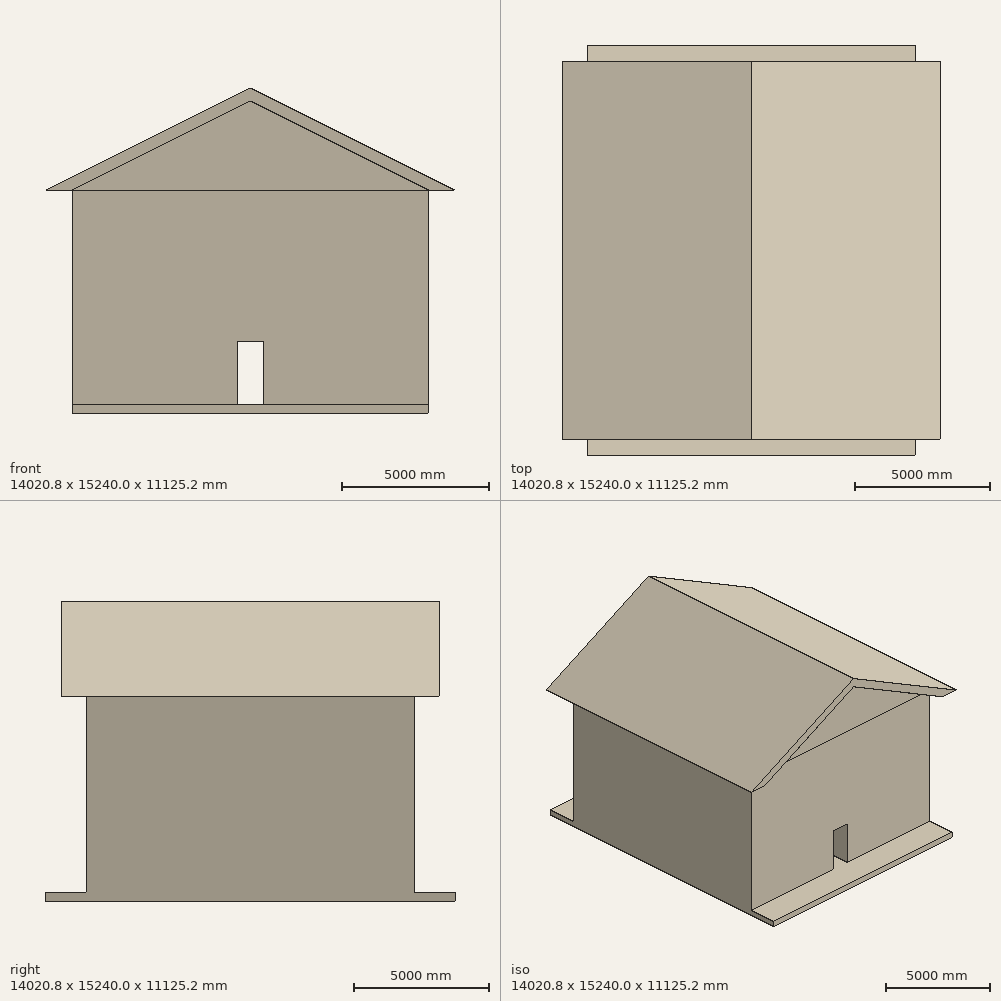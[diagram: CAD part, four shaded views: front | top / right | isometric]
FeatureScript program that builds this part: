
annotation { "Feature Type Name" : "Feature", "Feature Type Description" : "" }
export const myFeature = defineFeature(function(context is Context, id is Id, definition is map)
    precondition{}
    {
        {
            var Q0;
            Q0=qCreatedBy(makeId("Front.planeOp"),FACE);
            var sketch = newSketch(context, id + "F0", { "sketchPlane" : qUnion([Q0])});
            skLineSegment(sketch, "E0", {"start": v(0, 0) * mm, "end": v(-6096, 0) * mm});
            skLineSegment(sketch, "E1", {"start": v(0, 0) * mm, "end": v(6096, 0) * mm});
            skLineSegment(sketch, "E2", {"start": v(0, 0) * mm, "end": v(0, 3048) * mm});
            skLineSegment(sketch, "E3", {"start": v(-6096, 0) * mm, "end": v(0, 3048) * mm});
            skLineSegment(sketch, "E4", {"start": v(6096, 0) * mm, "end": v(0, 3048) * mm});
            skLineSegment(sketch, "E5", {"start": v(-6096, 0) * mm, "end": v(-7010.4, 0) * mm});
            skLineSegment(sketch, "E6", {"start": v(6096, 0) * mm, "end": v(7010.4, 0) * mm});
            skLineSegment(sketch, "E7", {"start": v(0, 3048) * mm, "end": v(0, 3505.2) * mm});
            skLineSegment(sketch, "E8", {"start": v(0, 3505.2) * mm, "end": v(7010.4, 0) * mm});
            skLineSegment(sketch, "E9", {"start": v(0, 3505.2) * mm, "end": v(-7010.4, 0) * mm});
            skLineSegment(sketch, "E10", {"start": v(-6096, 0) * mm, "end": v(-6096, -7315.2) * mm});
            skLineSegment(sketch, "E11", {"start": v(6096, 0) * mm, "end": v(6096, -7315.2) * mm});
            skLineSegment(sketch, "E12", {"start": v(-6096, -7315.2) * mm, "end": v(6096, -7315.2) * mm});
            skLineSegment(sketch, "E13", {"start": v(-6096, -7315.2) * mm, "end": v(-6096, -7620) * mm});
            skLineSegment(sketch, "E14", {"start": v(6096, -7315.2) * mm, "end": v(6096, -7620) * mm});
            skLineSegment(sketch, "E15", {"start": v(6096, -7620) * mm, "end": v(-6096, -7620) * mm});
            skLineSegment(sketch, "E16", {"start": v(0, -7315.2) * mm, "end": v(-457.2, -7315.2) * mm});
            skLineSegment(sketch, "E17", {"start": v(-457.2, -7315.2) * mm, "end": v(0, -7315.2) * mm});
            skLineSegment(sketch, "E18", {"start": v(0, -7315.2) * mm, "end": v(457.2, -7315.2) * mm});
            skLineSegment(sketch, "E19", {"start": v(457.2, -7315.2) * mm, "end": v(457.2, -5181.6) * mm});
            skLineSegment(sketch, "E20", {"start": v(457.2, -5181.6) * mm, "end": v(-457.2, -5181.6) * mm});
            skLineSegment(sketch, "E21", {"start": v(-457.2, -7315.2) * mm, "end": v(-457.2, -5181.6) * mm});
            skSolve(sketch);
        }
        {
            var Q0;
            Q0=makeQuery(id+"F0.imprint","IMPRINT",FACE,{"disambiguationData":[TD([[makeQuery(id+"F0.imprint","IMPRINT",EDGE,{"derivedFrom":sQuery(id+"F0.wireOp",EDGE,"E3")}),1.0]])]});
            var Q1;
            Q1=makeQuery(id+"F0.imprint","IMPRINT",FACE,{"disambiguationData":[TD([[makeQuery(id+"F0.imprint","IMPRINT",EDGE,{"derivedFrom":sQuery(id+"F0.wireOp",EDGE,"E4")}),-1.0]])]});
            extrude(context, id + "F1", {"entities" : qUnion([Q0, Q1]), "endBound" : BoundingType.SYMMETRIC, "depth" : 14020.8 * mm, "offsetDistance" : 30.48 * mm});
        }
        {
            var Q0;
            Q0=makeQuery(id+"F0.imprint","IMPRINT",FACE,{"disambiguationData":[TD([[makeQuery(id+"F0.imprint","IMPRINT",EDGE,{"derivedFrom":sQuery(id+"F0.wireOp",EDGE,"E0")}),1.0]])]});
            extrude(context, id + "F2", {"entities" : qUnion([Q0]), "endBound" : BoundingType.SYMMETRIC, "depth" : 12192 * mm, "offsetDistance" : 30.48 * mm});
        }
        {
            var Q0;
            Q0=makeQuery(id+"F0.imprint","IMPRINT",FACE,{"disambiguationData":[TD([[makeQuery(id+"F0.imprint","IMPRINT",EDGE,{"derivedFrom":sQuery(id+"F0.wireOp",EDGE,"E0")}),-1.0]])]});
            var Q1;
            Q1=makeQuery(id+"F0.imprint","IMPRINT",FACE,{"disambiguationData":[TD([[makeQuery(id+"F0.imprint","IMPRINT",EDGE,{"derivedFrom":sQuery(id+"F0.wireOp",EDGE,"E1")}),1.0]])]});
            extrude(context, id + "F3", {"entities" : qUnion([Q0, Q1]), "endBound" : BoundingType.SYMMETRIC, "depth" : 12192 * mm, "offsetDistance" : 30.48 * mm});
        }
        {
            var Q0;
            {var subQ1=sQuery(id+"F0.wireOp",EDGE,"E13");Q0=makeQuery(id+"F0.imprint","IMPRINT",FACE,{"disambiguationData":[TD([[makeQuery(id+"F0.imprint","IMPRINT",EDGE,{"derivedFrom":subQ1}),1.0]])]});}
            extrude(context, id + "F4", {"entities" : qUnion([Q0]), "operationType" : NewBodyOperationType.ADD, "endBound" : BoundingType.SYMMETRIC, "depth" : 15240 * mm, "offsetDistance" : 30.48 * mm});
        }
    });
